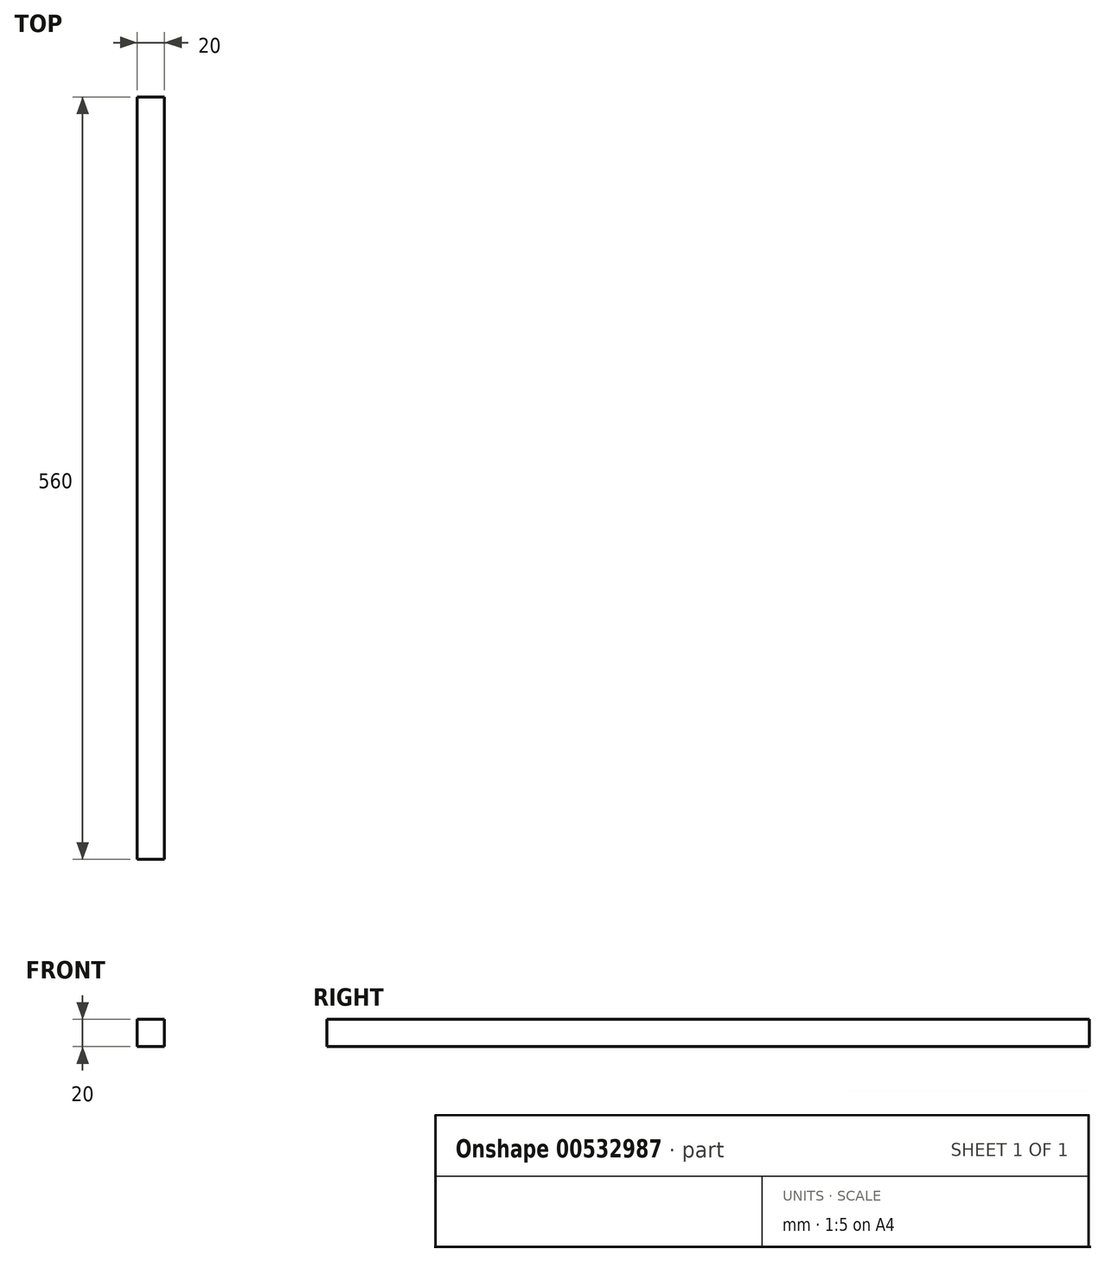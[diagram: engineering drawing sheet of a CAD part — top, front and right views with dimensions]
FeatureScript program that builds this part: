
annotation { "Feature Type Name" : "Feature", "Feature Type Description" : "" }
export const myFeature = defineFeature(function(context is Context, id is Id, definition is map)
    precondition{}
    {
        {
            var Q0;
            Q0=qCreatedBy(makeId("Front.planeOp"),FACE);
            var sketch = newSketch(context, id + "F0", { "sketchPlane" : qUnion([Q0])});
            skLineSegment(sketch, "E0.bottom", {"start": v(27.21, 0) * mm, "end": v(47.21, 0) * mm});
            skLineSegment(sketch, "E0.top", {"start": v(27.21, -20) * mm, "end": v(47.21, -20) * mm});
            skLineSegment(sketch, "E0.left", {"start": v(27.21, 0) * mm, "end": v(27.21, -20) * mm});
            skLineSegment(sketch, "E0.right", {"start": v(47.21, 0) * mm, "end": v(47.21, -20) * mm});
            skSolve(sketch);
        }
        {
            var Q0;
            Q0 = qSketchRegion(id + "F0", true);
            var Q1;
            Q1=makeQuery(id+"F0.imprint","IMPRINT",FACE,{"disambiguationData":[TD([[makeQuery(id+"F0.imprint","IMPRINT",EDGE,{"derivedFrom":sQuery(id+"F0.wireOp",EDGE,"E0.bottom")}),-1.0]])]});
            extrude(context, id + "F1", {"entities" : qUnion([Q0, Q1]), "oppositeDirection" : true, "depth" : 560 * mm, "offsetDistance" : 25 * mm});
        }
    });
